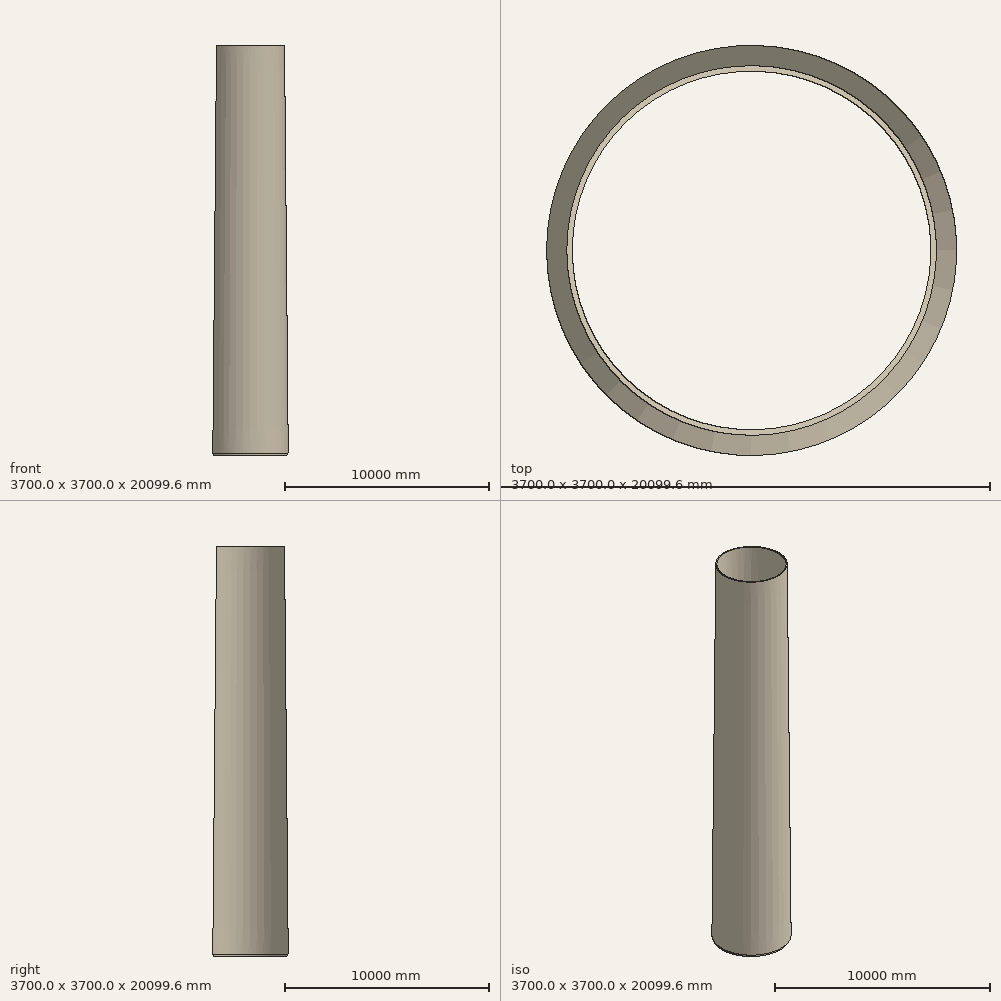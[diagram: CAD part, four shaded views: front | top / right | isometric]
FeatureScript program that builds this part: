
annotation { "Feature Type Name" : "Feature", "Feature Type Description" : "" }
export const myFeature = defineFeature(function(context is Context, id is Id, definition is map)
    precondition{}
    {
        {
            var Q0;
            Q0=qCreatedBy(makeId("Front.planeOp"),FACE);
            var sketch = newSketch(context, id + "F0", { "sketchPlane" : qUnion([Q0])});
            skLineSegment(sketch, "E0", {"start": v(-1787.5, -6912.5) * mm, "end": v(-1787.5, 15087.5) * mm, "construction": true});
            skLineSegment(sketch, "E1.bottom", {"start": v(212.5, -6912.5) * mm, "end": v(512.5, -6912.5) * mm});
            skLineSegment(sketch, "E1.top", {"start": v(262.5, -6812.5) * mm, "end": v(512.5, -6812.5) * mm});
            skLineSegment(sketch, "E1.left", {"start": v(212.5, -6912.5) * mm, "end": v(212.5, -6812.5) * mm});
            skLineSegment(sketch, "E1.right", {"start": v(512.5, -6912.5) * mm, "end": v(512.5, -6812.5) * mm});
            skLineSegment(sketch, "E2.bottom", {"start": v(12.5, 15087.5) * mm, "end": v(62.5, 15087.5) * mm});
            skLineSegment(sketch, "E3", {"start": v(12.5, 15087.5) * mm, "end": v(212.5, -6812.5) * mm});
            skLineSegment(sketch, "E4.0", {"start": v(62.5, 15087.5) * mm, "end": v(262.5, -6812.5) * mm});
            skSolve(sketch);
        }
        {
            var Q0;
            Q0=qCreatedBy(makeId("Front.planeOp"),FACE);
            var sketch = newSketch(context, id + "F1", { "sketchPlane" : qUnion([Q0])});
            skLineSegment(sketch, "E5", {"start": v(62.5, 15087.5) * mm, "end": v(12.5, 15087.5) * mm});
            skLineSegment(sketch, "E6", {"start": v(12.5, 15087.5) * mm, "end": v(-170.14, 35086.67) * mm});
            skLineSegment(sketch, "E7", {"start": v(62.5, 15087.5) * mm, "end": v(-120.14, 35086.67) * mm});
            skLineSegment(sketch, "E8", {"start": v(-120.14, 35086.67) * mm, "end": v(-170.14, 35086.67) * mm});
            skSolve(sketch);
        }
        {
            var Q0;
            Q0 = qSketchRegion(id + "F1", true);
            var Q1;
            Q1=sQuery(id+"F0.wireOp",EDGE,"E0");
            revolve(context, id + "F2", {"entities" : qUnion([Q0]), "axis" : qUnion([Q1]), "revolveType" : RevolveType.FULL});
        }
        {
            var Q0;
            Q0=qCreatedBy(makeId("Front.planeOp"),FACE);
            var sketch = newSketch(context, id + "F3", { "sketchPlane" : qUnion([Q0])});
            skLineSegment(sketch, "E9", {"start": v(62.5, 15087.5) * mm, "end": v(12.5, 15087.5) * mm});
            skLineSegment(sketch, "E10", {"start": v(-37.96, 15137.5) * mm, "end": v(62.04, 15137.5) * mm});
            skLineSegment(sketch, "E11", {"start": v(62.04, 15137.5) * mm, "end": v(62.5, 15087.5) * mm});
            skLineSegment(sketch, "E12.0", {"start": v(12.5, 15087.5) * mm, "end": v(13.41, 14987.5) * mm});
            skCircle(sketch, "E13", {"center": v(12.5, 15087.5) * mm, "radius": 100 * mm, "construction": true});
            skPoint(sketch, "E14.orphan", {"position": v(212.5, -6812.5) * mm});
            skLineSegment(sketch, "E15", {"start": v(13.41, 14987.5) * mm, "end": v(-36.58, 14987.05) * mm});
            skLineSegment(sketch, "E16", {"start": v(-37.96, 15137.5) * mm, "end": v(-36.58, 14987.05) * mm});
            skSolve(sketch);
        }
        {
            var Q0;
            Q0 = qSketchRegion(id + "F3", true);
            var Q1;
            Q1=sQuery(id+"F0.wireOp",EDGE,"E0");
            revolve(context, id + "F4", {"operationType" : NewBodyOperationType.ADD, "entities" : qUnion([Q0]), "axis" : qUnion([Q1]), "revolveType" : RevolveType.FULL});
        }
    });
